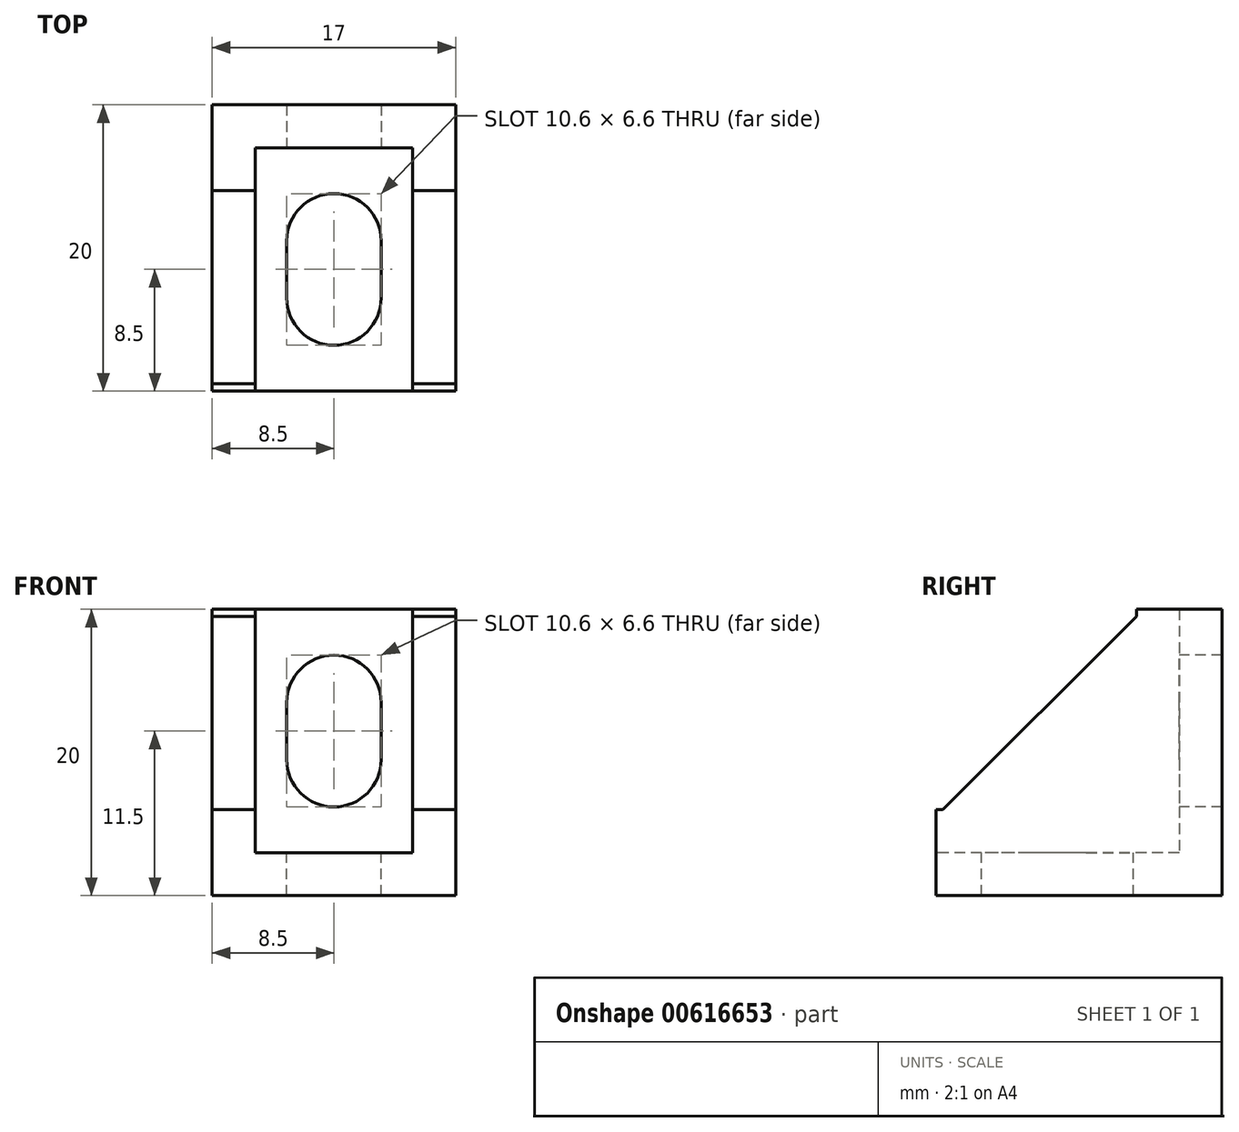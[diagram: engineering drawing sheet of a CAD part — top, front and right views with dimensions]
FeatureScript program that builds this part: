
annotation { "Feature Type Name" : "Feature", "Feature Type Description" : "" }
export const myFeature = defineFeature(function(context is Context, id is Id, definition is map)
    precondition{}
    {
        {
            assignVariable(context, id + "F0", {"name" : "length", "anyValue" : 20});
        }
        {
            assignVariable(context, id + "F1", {"name" : "thickness", "anyValue" : 3});
        }
        {
            var Q0;
            Q0=qCreatedBy(makeId("Top.planeOp"),FACE);
            var sketch = newSketch(context, id + "F2", { "sketchPlane" : qUnion([Q0])});
            skLineSegment(sketch, "E0.rect.bottom", {"start": v(8.5, 10) * mm, "end": v(-8.5, 10) * mm});
            skLineSegment(sketch, "E0.rect.top", {"start": v(8.5, -10) * mm, "end": v(-8.5, -10) * mm});
            skLineSegment(sketch, "E0.rect.left", {"start": v(8.5, 10) * mm, "end": v(8.5, -10) * mm});
            skLineSegment(sketch, "E0.rect.right", {"start": v(-8.5, 10) * mm, "end": v(-8.5, -10) * mm});
            skPoint(sketch, "E0.rect.middle", {"position": v(0, 0) * mm});
            skSolve(sketch);
        }
        {
            var Q0;
            Q0=makeQuery(id+"F2.imprint","IMPRINT",FACE,{"disambiguationData":[TD([[makeQuery(id+"F2.imprint","IMPRINT",EDGE,{"derivedFrom":sQuery(id+"F2.wireOp",EDGE,"E0.rect.bottom")}),1.0]])]});
            extrude(context, id + "F3", {"entities" : qUnion([Q0]), "depth" : (getVariable(context, 'thickness')) * mm, "offsetDistance" : 25 * mm});
        }
        {
            var Q0;
            Q0=makeQuery(id+"F3.opExtrude","CAP_FACE",FACE,{"disambiguationData":[OSD([sQuery(id+"F2.wireOp",EDGE,"E0.rect.bottom"),sQuery(id+"F2.wireOp",EDGE,"E0.rect.top"),sQuery(id+"F2.wireOp",EDGE,"E0.rect.left"),sQuery(id+"F2.wireOp",EDGE,"E0.rect.right")])],"isStart":false});
            var sketch = newSketch(context, id + "F4", { "sketchPlane" : qUnion([Q0])});
            skLineSegment(sketch, "E1", {"start": v(5.5, 7) * mm, "end": v(-5.5, 7) * mm});
            skLineSegment(sketch, "E2", {"start": v(-5.5, 7) * mm, "end": v(-5.5, -10) * mm});
            skLineSegment(sketch, "E3", {"start": v(5.5, 7) * mm, "end": v(5.5, -10) * mm});
            skLineSegment(sketch, "E4", {"start": v(5.5, -10) * mm, "end": v(8.5, -10) * mm});
            skLineSegment(sketch, "E5", {"start": v(8.5, -10) * mm, "end": v(8.5, 10) * mm});
            skLineSegment(sketch, "E6", {"start": v(8.5, 10) * mm, "end": v(-8.5, 10) * mm});
            skLineSegment(sketch, "E7", {"start": v(-8.5, 10) * mm, "end": v(-8.5, -10) * mm});
            skLineSegment(sketch, "E8", {"start": v(-8.5, -10) * mm, "end": v(-5.5, -10) * mm});
            skSolve(sketch);
        }
        {
            var Q0;
            Q0=makeQuery(id+"F4.imprint","IMPRINT",FACE,{"disambiguationData":[TD([[makeQuery(id+"F4.imprint","IMPRINT",EDGE,{"derivedFrom":sQuery(id+"F4.wireOp",EDGE,"E1")}),-1.0]])]});
            extrude(context, id + "F5", {"entities" : qUnion([Q0]), "operationType" : NewBodyOperationType.ADD, "depth" : (getVariable(context, 'length') - getVariable(context, 'thickness')) * mm, "offsetDistance" : 25 * mm});
        }
        {
            var Q0;
            Q0=makeQuery(id+"F5.boolean.opBoolean","MERGE",FACE,{"derivedFrom":[makeQuery(id+"F3.opExtrude","SWEPT_FACE",FACE,{"disambiguationData":[OSD([sQuery(id+"F2.wireOp",EDGE,"E0.rect.left")])]}),makeQuery(id+"F5.opExtrude","SWEPT_FACE",FACE,{"disambiguationData":[OSD([sQuery(id+"F4.wireOp",EDGE,"E5")])]})]});
            var sketch = newSketch(context, id + "F6", { "sketchPlane" : qUnion([Q0])});
            skLineSegment(sketch, "E9", {"start": v(-10, 0) * mm, "end": v(-10, 6) * mm});
            skLineSegment(sketch, "E10", {"start": v(-10, 6) * mm, "end": v(-9.5, 6) * mm});
            skLineSegment(sketch, "E11", {"start": v(-9.5, 6) * mm, "end": v(4, 19.5) * mm});
            skLineSegment(sketch, "E12", {"start": v(4, 19.5) * mm, "end": v(4, 20) * mm});
            skLineSegment(sketch, "E13", {"start": v(4, 20) * mm, "end": v(10, 20) * mm});
            skLineSegment(sketch, "E14", {"start": v(10, 20) * mm, "end": v(10, 0) * mm});
            skLineSegment(sketch, "E15", {"start": v(10, 0) * mm, "end": v(-10, 0) * mm});
            skLineSegment(sketch, "E16", {"start": v(-10, 6) * mm, "end": v(-10, 0) * mm});
            skSolve(sketch);
        }
        {
            var Q0;
            Q0=qSketchRegion(id+"F6",true);
            extrude(context, id + "F7", {"entities" : qUnion([Q0]), "operationType" : NewBodyOperationType.INTERSECT, "oppositeDirection" : true, "depth" : 25 * mm});
        }
        {
            var Q0;
            Q0=makeQuery(id+"F3.opExtrude","CAP_FACE",FACE,{"disambiguationData":[OSD([sQuery(id+"F2.wireOp",EDGE,"E0.rect.bottom"),sQuery(id+"F2.wireOp",EDGE,"E0.rect.top"),sQuery(id+"F2.wireOp",EDGE,"E0.rect.left"),sQuery(id+"F2.wireOp",EDGE,"E0.rect.right")])],"isStart":false});
            var sketch = newSketch(context, id + "F8", { "sketchPlane" : qUnion([Q0])});
            skLineSegment(sketch, "E17.rect.bottom", {"start": v(-3.3, 0.5) * mm, "end": v(3.3, 0.5) * mm});
            skLineSegment(sketch, "E17.rect.top", {"start": v(-3.3, -3.5) * mm, "end": v(3.3, -3.5) * mm});
            skLineSegment(sketch, "E17.rect.left", {"start": v(-3.3, 0.5) * mm, "end": v(-3.3, -3.5) * mm});
            skLineSegment(sketch, "E17.rect.right", {"start": v(3.3, 0.5) * mm, "end": v(3.3, -3.5) * mm});
            skPoint(sketch, "E17.rect.middle", {"position": v(0, -1.5) * mm});
            skArc(sketch, "E18", {"start": v(-3.3, -3.5) * mm, "mid": v(0, -6.8) * mm, "end": v(3.3, -3.5) * mm});
            skArc(sketch, "E19", {"start": v(3.3, 0.5) * mm, "mid": v(0, 3.8) * mm, "end": v(-3.3, 0.5) * mm});
            skSolve(sketch);
        }
        {
            var Q0;
            Q0=qSketchRegion(id+"F8",true);
            extrude(context, id + "F9", {"entities" : qUnion([Q0]), "operationType" : NewBodyOperationType.REMOVE, "oppositeDirection" : true, "depth" : 25 * mm});
        }
        {
            var Q0;
            Q0=makeQuery(id+"F5.opExtrude","SWEPT_FACE",FACE,{"disambiguationData":[OSD([sQuery(id+"F4.wireOp",EDGE,"E1")])]});
            var sketch = newSketch(context, id + "F10", { "sketchPlane" : qUnion([Q0])});
            skLineSegment(sketch, "E20.rect.bottom", {"start": v(3.3, 9.5) * mm, "end": v(-3.3, 9.5) * mm});
            skLineSegment(sketch, "E20.rect.top", {"start": v(3.3, 13.5) * mm, "end": v(-3.3, 13.5) * mm});
            skLineSegment(sketch, "E20.rect.left", {"start": v(3.3, 9.5) * mm, "end": v(3.3, 13.5) * mm});
            skLineSegment(sketch, "E20.rect.right", {"start": v(-3.3, 9.5) * mm, "end": v(-3.3, 13.5) * mm});
            skPoint(sketch, "E20.rect.middle", {"position": v(0, 11.5) * mm});
            skArc(sketch, "E21", {"start": v(-3.3, 9.5) * mm, "mid": v(0, 6.2) * mm, "end": v(3.3, 9.5) * mm});
            skArc(sketch, "E22", {"start": v(3.3, 13.5) * mm, "mid": v(0, 16.8) * mm, "end": v(-3.3, 13.5) * mm});
            skSolve(sketch);
        }
        {
            var Q0;
            Q0=qSketchRegion(id+"F10",true);
            extrude(context, id + "F11", {"entities" : qUnion([Q0]), "operationType" : NewBodyOperationType.REMOVE, "oppositeDirection" : true, "depth" : 25 * mm});
        }
    });
